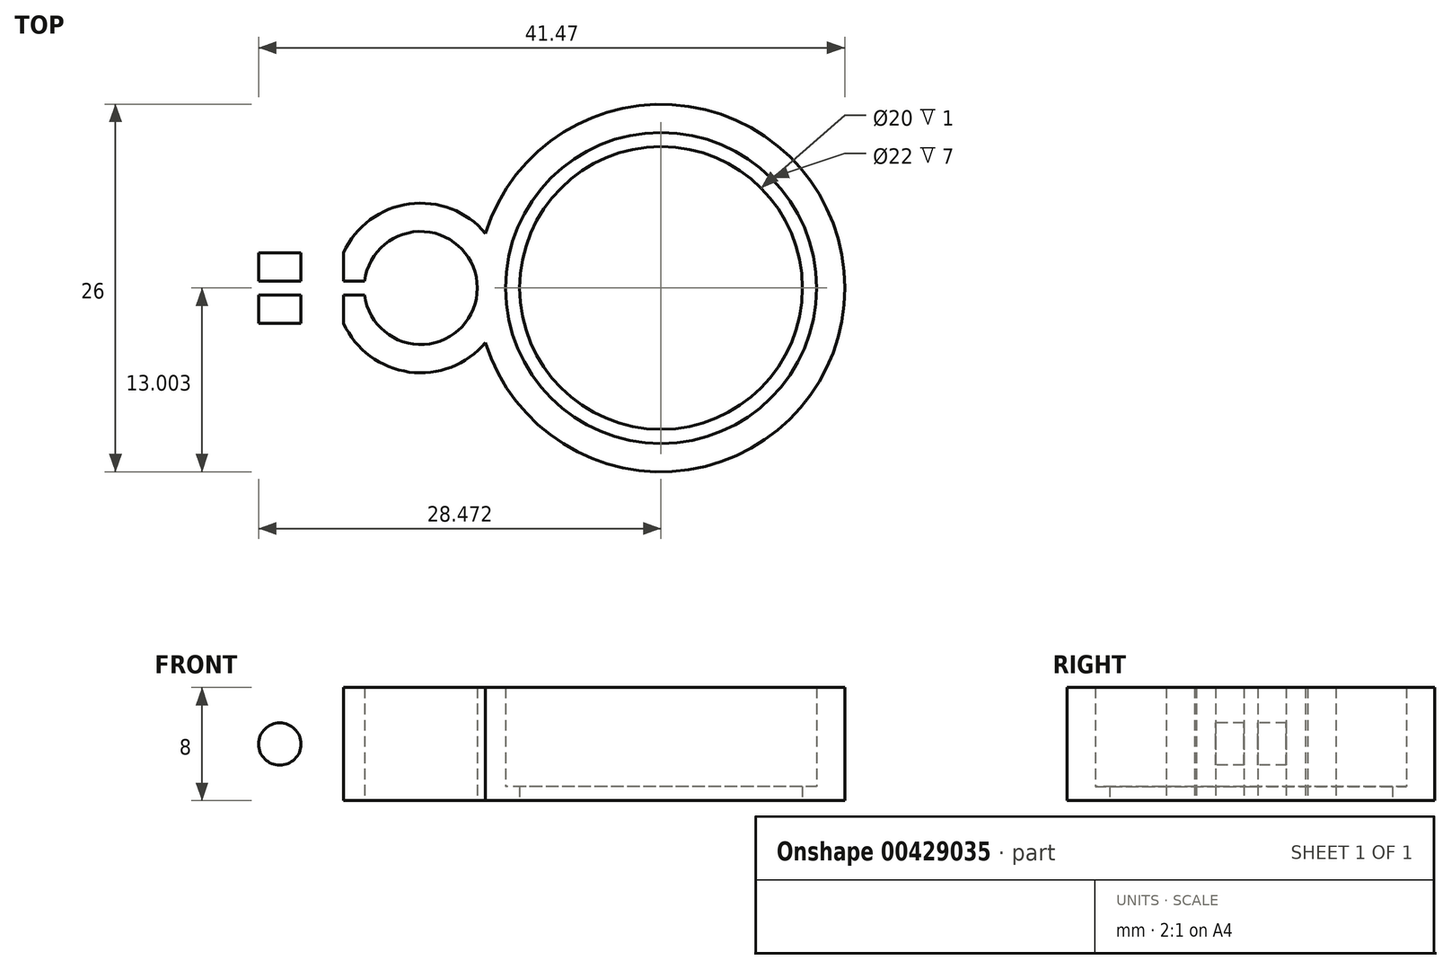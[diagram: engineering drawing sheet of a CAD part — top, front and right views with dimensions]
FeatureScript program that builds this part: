
annotation { "Feature Type Name" : "Feature", "Feature Type Description" : "" }
export const myFeature = defineFeature(function(context is Context, id is Id, definition is map)
    precondition{}
    {
        {
            var Q0;
            Q0=qCreatedBy(makeId("Top.planeOp"),FACE);
            var sketch = newSketch(context, id + "F0", { "sketchPlane" : qUnion([Q0])});
            skCircle(sketch, "E0", {"center": v(-35.7, 2.82) * mm, "radius": 10 * mm});
            skCircle(sketch, "E1", {"center": v(-35.7, 2.82) * mm, "radius": 11 * mm});
            skCircle(sketch, "E2", {"center": v(-35.7, 2.82) * mm, "radius": 13 * mm});
            skCircle(sketch, "E3", {"center": v(-35.7, 2.82) * mm, "radius": 4 * mm});
            skLineSegment(sketch, "E4", {"start": v(-35.7, 2.82) * mm, "end": v(-63.56, 2.82) * mm});
            skCircle(sketch, "E5", {"center": v(-52.7, 2.82) * mm, "radius": 4 * mm});
            skCircle(sketch, "E6", {"center": v(-52.7, 2.82) * mm, "radius": 6 * mm});
            skLineSegment(sketch, "E7.bottom", {"start": v(-56.2, 2.32) * mm, "end": v(-61.2, 2.32) * mm});
            skLineSegment(sketch, "E7.top", {"start": v(-56.2, 3.32) * mm, "end": v(-61.2, 3.32) * mm});
            skLineSegment(sketch, "E7.left", {"start": v(-56.2, 2.32) * mm, "end": v(-56.2, 3.32) * mm});
            skLineSegment(sketch, "E7.right", {"start": v(-61.2, 2.32) * mm, "end": v(-61.2, 3.32) * mm});
            skPoint(sketch, "E7.middle", {"position": v(-58.7, 2.82) * mm});
            skLineSegment(sketch, "E8.bottom", {"start": v(-56.67, 3.32) * mm, "end": v(-66.67, 3.32) * mm});
            skLineSegment(sketch, "E8.top", {"start": v(-56.67, 5.32) * mm, "end": v(-66.67, 5.32) * mm});
            skLineSegment(sketch, "E8.left", {"start": v(-56.67, 3.32) * mm, "end": v(-56.67, 5.32) * mm});
            skLineSegment(sketch, "E8.right", {"start": v(-66.67, 3.32) * mm, "end": v(-66.67, 5.32) * mm});
            skLineSegment(sketch, "E9.bottom", {"start": v(-56.67, 2.32) * mm, "end": v(-66.67, 2.32) * mm});
            skLineSegment(sketch, "E9.top", {"start": v(-56.67, 0.32) * mm, "end": v(-66.67, 0.32) * mm});
            skLineSegment(sketch, "E9.left", {"start": v(-56.67, 2.32) * mm, "end": v(-56.67, 0.32) * mm});
            skLineSegment(sketch, "E9.right", {"start": v(-66.67, 2.32) * mm, "end": v(-66.67, 0.32) * mm});
            skSolve(sketch);
        }
        {
            var Q0;
            Q0=makeQuery(id+"F0.imprint","IMPRINT",FACE,{"disambiguationData":[TD([[makeQuery(id+"F0.imprint","IMPRINT",EDGE,{"derivedFrom":sQuery(id+"F0.wireOp",EDGE,"E0")}),-1.0]])]});
            extrude(context, id + "F1", {"entities" : qUnion([Q0]), "depth" : 1 * mm});
        }
        {
            var Q0;
            {var subQ0=sQuery(id+"F0.wireOp",EDGE,"E8.right");Q0=makeQuery(id+"F0.imprint","IMPRINT",FACE,{"disambiguationData":[TD([[makeQuery(id+"F0.imprint","IMPRINT",EDGE,{"derivedFrom":subQ0}),-1.0]])]});}
            var Q1;
            {var subQ2=sQuery(id+"F0.wireOp",EDGE,"E9.right");Q1=makeQuery(id+"F0.imprint","IMPRINT",FACE,{"disambiguationData":[TD([[makeQuery(id+"F0.imprint","IMPRINT",EDGE,{"derivedFrom":subQ2}),1.0]])]});}
            var Q2;
            {var subQ5=sQuery(id+"F0.wireOp",EDGE,"E8.left");Q2=makeQuery(id+"F0.imprint","IMPRINT",FACE,{"disambiguationData":[TD([[makeQuery(id+"F0.imprint","IMPRINT",EDGE,{"derivedFrom":subQ5}),1.0]])]});}
            var Q3;
            {var subQ5=sQuery(id+"F0.wireOp",EDGE,"E9.left");Q3=makeQuery(id+"F0.imprint","IMPRINT",FACE,{"disambiguationData":[TD([[makeQuery(id+"F0.imprint","IMPRINT",EDGE,{"derivedFrom":subQ5}),-1.0]])]});}
            var Q4;
            {var subQ5=sQuery(id+"F0.wireOp",EDGE,"E8.left");Q4=makeQuery(id+"F0.imprint","IMPRINT",FACE,{"disambiguationData":[TD([[makeQuery(id+"F0.imprint","IMPRINT",EDGE,{"derivedFrom":subQ5}),-1.0]])]});}
            var Q5;
            {var subQ5=sQuery(id+"F0.wireOp",EDGE,"E9.left");Q5=makeQuery(id+"F0.imprint","IMPRINT",FACE,{"disambiguationData":[TD([[makeQuery(id+"F0.imprint","IMPRINT",EDGE,{"derivedFrom":subQ5}),1.0]])]});}
            var Q6;
            {var subQ0=sQuery(id+"F0.wireOp",EDGE,"E1");Q6=makeQuery(id+"F0.imprint","IMPRINT",FACE,{"disambiguationData":[TD([[makeQuery(id+"F0.imprint","IMPRINT",EDGE,{"derivedFrom":subQ0}),-1.0]])]});}
            var Q7;
            {var subQ0=sQuery(id+"F0.wireOp",EDGE,"E6");var subQ1=sQuery(id+"F0.wireOp",EDGE,"E2");var subQ2=makeQuery(id+"F0.imprint","INTERSECT",VERTEX,{"disambiguationData":[OD(1.0)],"derivedFrom":[subQ1,subQ0]});Q7=makeQuery(id+"F0.imprint","IMPRINT",FACE,{"disambiguationData":[TD([[makeQuery(id+"F0.imprint","IMPRINT",EDGE,{"disambiguationData":[TD([[subQ2,1.0]])],"derivedFrom":subQ1}),1.0]])]});}
            var Q8;
            {var subQ0=sQuery(id+"F0.wireOp",EDGE,"E6");var subQ1=sQuery(id+"F0.wireOp",EDGE,"E2");var subQ2=makeQuery(id+"F0.imprint","INTERSECT",VERTEX,{"disambiguationData":[OD(0.0)],"derivedFrom":[subQ1,subQ0]});Q8=makeQuery(id+"F0.imprint","IMPRINT",FACE,{"disambiguationData":[TD([[makeQuery(id+"F0.imprint","IMPRINT",EDGE,{"disambiguationData":[TD([[subQ2,-1.0]])],"derivedFrom":subQ1}),1.0]])]});}
            extrude(context, id + "F2", {"entities" : qUnion([Q0, Q1, Q2, Q3, Q4, Q5, Q6, Q7, Q8]), "operationType" : NewBodyOperationType.ADD, "depth" : 8 * mm});
        }
        {
            var Q0;
            Q0=makeQuery(id+"F2.opExtrude","SWEPT_FACE",FACE,{"disambiguationData":[OSD([sQuery(id+"F0.wireOp",EDGE,"E9.top")])]});
            var sketch = newSketch(context, id + "F3", { "sketchPlane" : qUnion([Q0])});
            skLineSegment(sketch, "E10", {"start": v(-66.67, 4) * mm, "end": v(-58.15, 4) * mm});
            skCircle(sketch, "E11", {"center": v(-62.67, 4) * mm, "radius": 1.5 * mm});
            skSolve(sketch);
        }
        {
            var Q0;
            Q0=makeQuery(id+"F2.opExtrude","CAP_EDGE",EDGE,{"disambiguationData":[OSD([sQuery(id+"F0.wireOp",EDGE,"E8.right")])],"isStart":false});
            var Q1;
            Q1=makeQuery(id+"F2.opExtrude","CAP_EDGE",EDGE,{"disambiguationData":[OSD([sQuery(id+"F0.wireOp",EDGE,"E9.right")])],"isStart":false});
            var Q2;
            Q2=makeQuery(id+"F2.opExtrude","CAP_EDGE",EDGE,{"disambiguationData":[OSD([sQuery(id+"F0.wireOp",EDGE,"E8.right")])],"isStart":true});
            var Q3;
            Q3=makeQuery(id+"F2.opExtrude","CAP_EDGE",EDGE,{"disambiguationData":[OSD([sQuery(id+"F0.wireOp",EDGE,"E9.right")])],"isStart":true});
            fillet(context, id + "F4", {"entities" : qUnion([Q0, Q1, Q2, Q3]), "radius" : 4 * mm, "tangentPropagation" : true, "allowEdgeOverflow" : false});
        }
        {
            var Q0;
            {var subQ0=sQuery(id+"F3.wireOp",EDGE,"E11");var subQ1=sQuery(id+"F3.wireOp",EDGE,"E10");var subQ2=makeQuery(id+"F3.imprint","INTERSECT",VERTEX,{"disambiguationData":[OD(0.0)],"derivedFrom":[subQ1,subQ0]});Q0=makeQuery(id+"F3.imprint","IMPRINT",FACE,{"disambiguationData":[TD([[makeQuery(id+"F3.imprint","IMPRINT",EDGE,{"disambiguationData":[TD([[subQ2,-1.0]])],"derivedFrom":subQ1}),1.0]])]});}
            var Q1;
            {var subQ0=sQuery(id+"F3.wireOp",EDGE,"E11");var subQ1=sQuery(id+"F3.wireOp",EDGE,"E10");var subQ2=makeQuery(id+"F3.imprint","INTERSECT",VERTEX,{"disambiguationData":[OD(0.0)],"derivedFrom":[subQ1,subQ0]});Q1=makeQuery(id+"F3.imprint","IMPRINT",FACE,{"disambiguationData":[TD([[makeQuery(id+"F3.imprint","IMPRINT",EDGE,{"disambiguationData":[TD([[subQ2,-1.0]])],"derivedFrom":subQ1}),-1.0]])]});}
            extrude(context, id + "F5", {"entities" : qUnion([Q0, Q1]), "operationType" : NewBodyOperationType.REMOVE, "oppositeDirection" : true, "depth" : 5 * mm});
        }
    });
